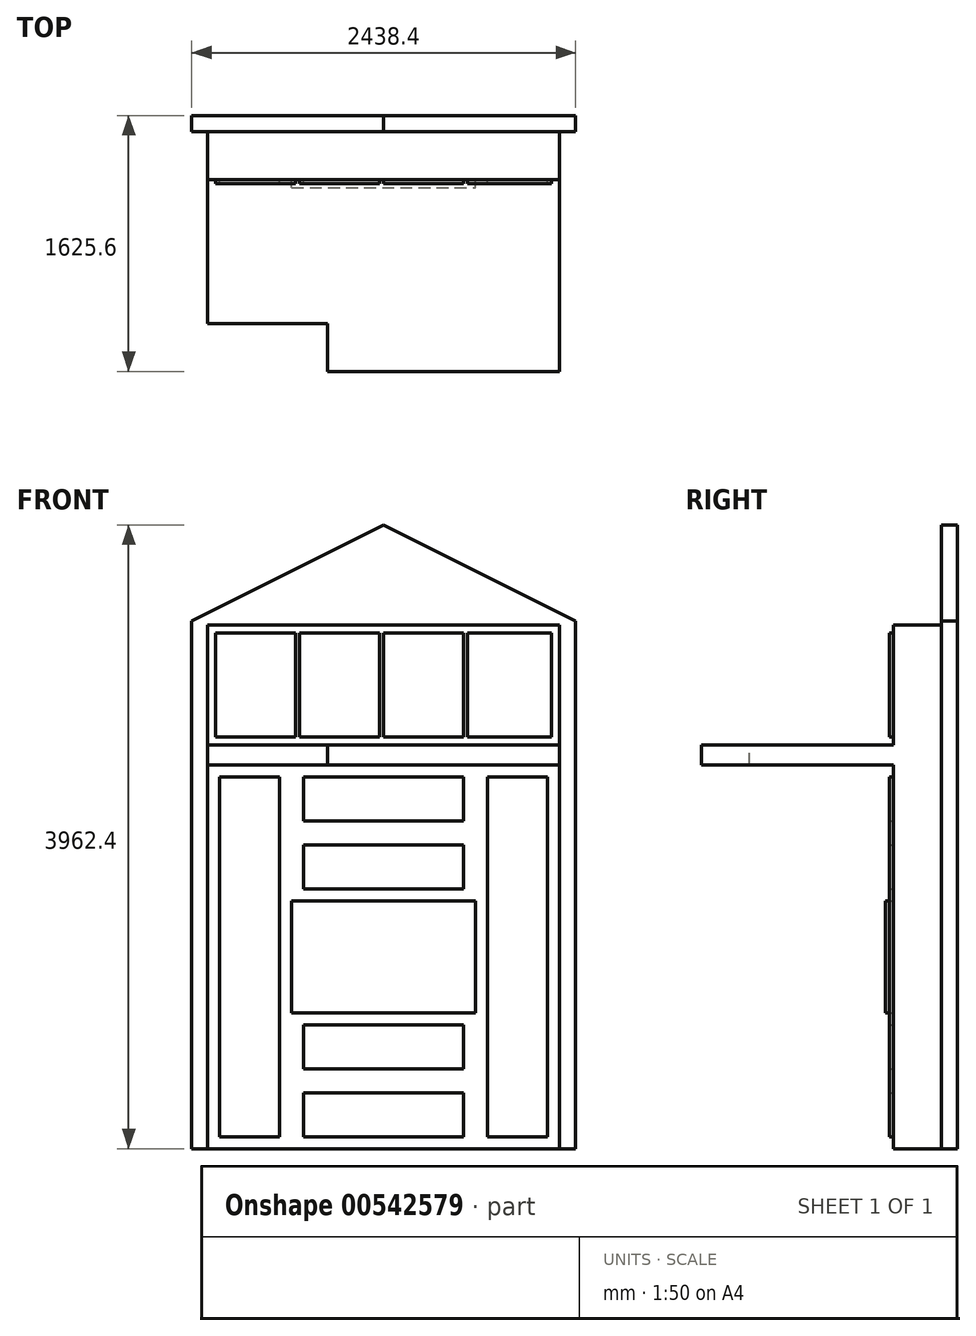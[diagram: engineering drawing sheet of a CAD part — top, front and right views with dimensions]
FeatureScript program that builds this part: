
annotation { "Feature Type Name" : "Feature", "Feature Type Description" : "" }
export const myFeature = defineFeature(function(context is Context, id is Id, definition is map)
    precondition{}
    {
        {
            var Q0;
            Q0=qCreatedBy(makeId("Front.planeOp"),FACE);
            var sketch = newSketch(context, id + "F0", { "sketchPlane" : qUnion([Q0])});
            skLineSegment(sketch, "E0.bottom", {"start": v(0, 0) * mm, "end": v(-2438.4, 0) * mm});
            skLineSegment(sketch, "E0.top", {"start": v(0, 3352.8) * mm, "end": v(-2438.4, 3352.8) * mm});
            skLineSegment(sketch, "E0.left", {"start": v(0, 0) * mm, "end": v(0, 3352.8) * mm});
            skLineSegment(sketch, "E0.right", {"start": v(-2438.4, 0) * mm, "end": v(-2438.4, 3352.8) * mm});
            skPoint(sketch, "E1", {"position": v(-2438.4, 2438.4) * mm});
            skLineSegment(sketch, "E2.bottom", {"start": v(-2438.4, 3352.8) * mm, "end": v(0, 3352.8) * mm, "construction": true});
            skLineSegment(sketch, "E2.top", {"start": v(-2438.4, 3962.4) * mm, "end": v(0, 3962.4) * mm, "construction": true});
            skLineSegment(sketch, "E2.left", {"start": v(-2438.4, 3352.8) * mm, "end": v(-2438.4, 3962.4) * mm, "construction": true});
            skLineSegment(sketch, "E2.right", {"start": v(0, 3352.8) * mm, "end": v(0, 3962.4) * mm, "construction": true});
            skPoint(sketch, "E3", {"position": v(-1219.2, 3962.4) * mm});
            skLineSegment(sketch, "E4", {"start": v(-2438.4, 3352.8) * mm, "end": v(-1219.2, 3962.4) * mm});
            skLineSegment(sketch, "E5", {"start": v(0, 3352.8) * mm, "end": v(-1219.2, 3962.4) * mm});
            skSolve(sketch);
        }
        {
            var Q0;
            Q0=makeQuery(id+"F0.imprint","IMPRINT",FACE,{"disambiguationData":[TD([[makeQuery(id+"F0.imprint","IMPRINT",EDGE,{"derivedFrom":sQuery(id+"F0.wireOp",EDGE,"E0.bottom")}),-1.0]])]});
            var Q1;
            Q1=makeQuery(id+"F0.imprint","IMPRINT",FACE,{"disambiguationData":[TD([[makeQuery(id+"F0.imprint","IMPRINT",EDGE,{"derivedFrom":sQuery(id+"F0.wireOp",EDGE,"E0.top")}),-1.0]])]});
            extrude(context, id + "F1", {"entities" : qUnion([Q0, Q1]), "oppositeDirection" : true, "depth" : 101.6 * mm, "offsetDistance" : 30.48 * mm});
        }
        {
            var Q0;
            Q0=makeQuery(id+"F1.opExtrude","CAP_FACE",FACE,{"disambiguationData":[OSD([sQuery(id+"F0.wireOp",EDGE,"E0.bottom"),sQuery(id+"F0.wireOp",EDGE,"E0.left"),sQuery(id+"F0.wireOp",EDGE,"E0.right"),sQuery(id+"F0.wireOp",EDGE,"E4"),sQuery(id+"F0.wireOp",EDGE,"E5")])],"isStart":true});
            var sketch = newSketch(context, id + "F2", { "sketchPlane" : qUnion([Q0])});
            skLineSegment(sketch, "E6.bottom", {"start": v(-2438.4, 0) * mm, "end": v(0, 0) * mm, "construction": true});
            skLineSegment(sketch, "E6.top", {"start": v(-2438.4, 0) * mm, "end": v(0, 0) * mm, "construction": true});
            skLineSegment(sketch, "E6.left", {"start": v(-2438.4, 0) * mm, "end": v(-2438.4, 0) * mm});
            skLineSegment(sketch, "E6.right", {"start": v(0, 0) * mm, "end": v(0, 0) * mm});
            skLineSegment(sketch, "E7", {"start": v(-2438.4, 2438.4) * mm, "end": v(-2336.8, 2438.4) * mm, "construction": true});
            skLineSegment(sketch, "E8", {"start": v(0, 1378.48) * mm, "end": v(-101.6, 1378.48) * mm, "construction": true});
            skLineSegment(sketch, "E9.bottom", {"start": v(-2336.8, 2438.4) * mm, "end": v(-101.6, 2438.4) * mm});
            skLineSegment(sketch, "E9.top", {"start": v(-2336.8, 0) * mm, "end": v(-101.6, 0) * mm});
            skLineSegment(sketch, "E9.left", {"start": v(-2336.8, 2438.4) * mm, "end": v(-2336.8, 0) * mm});
            skLineSegment(sketch, "E9.right", {"start": v(-101.6, 2438.4) * mm, "end": v(-101.6, 0) * mm});
            skSolve(sketch);
        }
        {
            var Q0;
            Q0=makeQuery(id+"F2.imprint","IMPRINT",FACE,{"disambiguationData":[TD([[makeQuery(id+"F2.imprint","IMPRINT",EDGE,{"derivedFrom":sQuery(id+"F2.wireOp",EDGE,"E9.bottom")}),-1.0]])]});
            extrude(context, id + "F3", {"entities" : qUnion([Q0]), "operationType" : NewBodyOperationType.ADD, "depth" : 304.8 * mm, "offsetDistance" : 30.48 * mm});
        }
        {
            var Q0;
            Q0=makeQuery(id+"F3.opExtrude","CAP_FACE",FACE,{"disambiguationData":[OSD([sQuery(id+"F2.wireOp",EDGE,"E9.bottom"),sQuery(id+"F2.wireOp",EDGE,"E9.top"),sQuery(id+"F2.wireOp",EDGE,"E9.left"),sQuery(id+"F2.wireOp",EDGE,"E9.right")])],"isStart":false});
            var sketch = newSketch(context, id + "F4", { "sketchPlane" : qUnion([Q0])});
            skLineSegment(sketch, "E10", {"start": v(-1219.2, 0) * mm, "end": v(-1219.2, 2438.4) * mm, "construction": true});
            skLineSegment(sketch, "E11", {"start": v(-2336.8, 1219.2) * mm, "end": v(-101.6, 1219.2) * mm, "construction": true});
            skLineSegment(sketch, "E12.bottom", {"start": v(-1803.4, 1574.8) * mm, "end": v(-635, 1574.8) * mm});
            skLineSegment(sketch, "E12.top", {"start": v(-1803.4, 863.6) * mm, "end": v(-635, 863.6) * mm});
            skLineSegment(sketch, "E12.left", {"start": v(-1803.4, 1574.8) * mm, "end": v(-1803.4, 863.6) * mm});
            skLineSegment(sketch, "E12.right", {"start": v(-635, 1574.8) * mm, "end": v(-635, 863.6) * mm});
            skPoint(sketch, "E12.middle", {"position": v(-1219.2, 1219.2) * mm});
            skSolve(sketch);
        }
        {
            var Q0;
            Q0=makeQuery(id+"F4.imprint","IMPRINT",FACE,{"disambiguationData":[TD([[makeQuery(id+"F4.imprint","IMPRINT",EDGE,{"derivedFrom":sQuery(id+"F4.wireOp",EDGE,"E12.bottom")}),-1.0]])]});
            extrude(context, id + "F5", {"entities" : qUnion([Q0]), "operationType" : NewBodyOperationType.ADD, "depth" : 50.8 * mm, "offsetDistance" : 30.48 * mm});
        }
        {
            var Q0;
            Q0=makeQuery(id+"F3.opExtrude","CAP_FACE",FACE,{"disambiguationData":[OSD([sQuery(id+"F2.wireOp",EDGE,"E9.bottom"),sQuery(id+"F2.wireOp",EDGE,"E9.top"),sQuery(id+"F2.wireOp",EDGE,"E9.left"),sQuery(id+"F2.wireOp",EDGE,"E9.right")])],"isStart":false});
            var sketch = newSketch(context, id + "F6", { "sketchPlane" : qUnion([Q0])});
            skLineSegment(sketch, "E13.bottom", {"start": v(-2336.8, 2438.4) * mm, "end": v(-101.6, 2438.4) * mm});
            skLineSegment(sketch, "E13.top", {"start": v(-2336.8, 0) * mm, "end": v(-101.6, 0) * mm});
            skLineSegment(sketch, "E13.left", {"start": v(-2336.8, 2438.4) * mm, "end": v(-2336.8, 0) * mm});
            skLineSegment(sketch, "E13.right", {"start": v(-101.6, 2438.4) * mm, "end": v(-101.6, 0) * mm});
            skLineSegment(sketch, "E14.bottom", {"start": v(-2336.8, 2438.4) * mm, "end": v(-1803.4, 2438.4) * mm, "construction": true});
            skLineSegment(sketch, "E14.top", {"start": v(-2336.8, 0) * mm, "end": v(-1803.4, 0) * mm, "construction": true});
            skLineSegment(sketch, "E14.left", {"start": v(-2336.8, 2438.4) * mm, "end": v(-2336.8, 0) * mm, "construction": true});
            skLineSegment(sketch, "E14.right", {"start": v(-1803.4, 2438.4) * mm, "end": v(-1803.4, 0) * mm});
            skLineSegment(sketch, "E15.bottom", {"start": v(-101.6, 0) * mm, "end": v(-635, 0) * mm});
            skLineSegment(sketch, "E15.top", {"start": v(-101.6, 2438.4) * mm, "end": v(-635, 2438.4) * mm});
            skLineSegment(sketch, "E15.left", {"start": v(-101.6, 0) * mm, "end": v(-101.6, 2438.4) * mm});
            skLineSegment(sketch, "E15.right", {"start": v(-635, 0) * mm, "end": v(-635, 2438.4) * mm});
            skLineSegment(sketch, "E16.bottom", {"start": v(-1803.4, 2438.4) * mm, "end": v(-635, 2438.4) * mm});
            skLineSegment(sketch, "E16.top", {"start": v(-1803.4, 2006.6) * mm, "end": v(-635, 2006.6) * mm});
            skLineSegment(sketch, "E16.left", {"start": v(-1803.4, 2438.4) * mm, "end": v(-1803.4, 2006.6) * mm});
            skLineSegment(sketch, "E16.right", {"start": v(-635, 2438.4) * mm, "end": v(-635, 2006.6) * mm, "construction": true});
            skLineSegment(sketch, "E17.bottom", {"start": v(-1803.4, 863.6) * mm, "end": v(-635, 863.6) * mm, "construction": true});
            skLineSegment(sketch, "E17.top", {"start": v(-1803.4, 431.8) * mm, "end": v(-635, 431.8) * mm});
            skLineSegment(sketch, "E17.left", {"start": v(-1803.4, 863.6) * mm, "end": v(-1803.4, 431.8) * mm});
            skLineSegment(sketch, "E17.right", {"start": v(-635, 863.6) * mm, "end": v(-635, 431.8) * mm});
            skLineSegment(sketch, "E18.0", {"start": v(-1879.6, 2362.2) * mm, "end": v(-1879.6, 76.2) * mm});
            skLineSegment(sketch, "E18.1", {"start": v(-2260.6, 2362.2) * mm, "end": v(-1879.6, 2362.2) * mm});
            skLineSegment(sketch, "E18.2", {"start": v(-2260.6, 2362.2) * mm, "end": v(-2260.6, 76.2) * mm});
            skLineSegment(sketch, "E18.3", {"start": v(-2260.6, 76.2) * mm, "end": v(-1879.6, 76.2) * mm});
            skPoint(sketch, "E19", {"position": v(-635, 431.8) * mm});
            skPoint(sketch, "E20", {"position": v(-635, 863.6) * mm});
            skPoint(sketch, "E21", {"position": v(-635, 2006.6) * mm});
            skPoint(sketch, "E22", {"position": v(-635, 1574.8) * mm});
            skLineSegment(sketch, "E23.bottom", {"start": v(-1727.2, 2362.2) * mm, "end": v(-711.2, 2362.2) * mm});
            skLineSegment(sketch, "E23.top", {"start": v(-1727.2, 2082.8) * mm, "end": v(-711.2, 2082.8) * mm});
            skLineSegment(sketch, "E23.left", {"start": v(-1727.2, 2362.2) * mm, "end": v(-1727.2, 2082.8) * mm});
            skLineSegment(sketch, "E23.right", {"start": v(-711.2, 2362.2) * mm, "end": v(-711.2, 2082.8) * mm});
            skLineSegment(sketch, "E24.bottom", {"start": v(-1727.2, 1930.4) * mm, "end": v(-711.2, 1930.4) * mm});
            skLineSegment(sketch, "E24.top", {"start": v(-1727.2, 1651) * mm, "end": v(-711.2, 1651) * mm});
            skLineSegment(sketch, "E24.left", {"start": v(-1727.2, 1930.4) * mm, "end": v(-1727.2, 1651) * mm});
            skLineSegment(sketch, "E24.right", {"start": v(-711.2, 1930.4) * mm, "end": v(-711.2, 1651) * mm});
            skLineSegment(sketch, "E25.bottom", {"start": v(-177.8, 2362.2) * mm, "end": v(-558.8, 2362.2) * mm});
            skLineSegment(sketch, "E25.top", {"start": v(-177.8, 76.2) * mm, "end": v(-558.8, 76.2) * mm});
            skLineSegment(sketch, "E25.left", {"start": v(-177.8, 2362.2) * mm, "end": v(-177.8, 76.2) * mm});
            skLineSegment(sketch, "E25.right", {"start": v(-558.8, 2362.2) * mm, "end": v(-558.8, 76.2) * mm});
            skLineSegment(sketch, "E26.bottom", {"start": v(-711.2, 76.2) * mm, "end": v(-1727.2, 76.2) * mm});
            skLineSegment(sketch, "E26.top", {"start": v(-711.2, 355.6) * mm, "end": v(-1727.2, 355.6) * mm});
            skLineSegment(sketch, "E26.left", {"start": v(-711.2, 76.2) * mm, "end": v(-711.2, 355.6) * mm});
            skLineSegment(sketch, "E26.right", {"start": v(-1727.2, 76.2) * mm, "end": v(-1727.2, 355.6) * mm});
            skLineSegment(sketch, "E27.bottom", {"start": v(-1727.2, 787.4) * mm, "end": v(-711.2, 787.4) * mm});
            skLineSegment(sketch, "E27.top", {"start": v(-1727.2, 508) * mm, "end": v(-711.2, 508) * mm});
            skLineSegment(sketch, "E27.left", {"start": v(-1727.2, 787.4) * mm, "end": v(-1727.2, 508) * mm});
            skLineSegment(sketch, "E27.right", {"start": v(-711.2, 787.4) * mm, "end": v(-711.2, 508) * mm});
            skSolve(sketch);
        }
        {
            var Q0;
            Q0=makeQuery(id+"F6.imprint","IMPRINT",FACE,{"disambiguationData":[TD([[makeQuery(id+"F6.imprint","IMPRINT",EDGE,{"derivedFrom":sQuery(id+"F6.wireOp",EDGE,"E25.bottom")}),1.0]])]});
            var Q1;
            Q1=makeQuery(id+"F6.imprint","IMPRINT",FACE,{"disambiguationData":[TD([[makeQuery(id+"F6.imprint","IMPRINT",EDGE,{"derivedFrom":sQuery(id+"F6.wireOp",EDGE,"E23.bottom")}),-1.0]])]});
            var Q2;
            Q2=makeQuery(id+"F6.imprint","IMPRINT",FACE,{"disambiguationData":[TD([[makeQuery(id+"F6.imprint","IMPRINT",EDGE,{"derivedFrom":sQuery(id+"F6.wireOp",EDGE,"E24.bottom")}),-1.0]])]});
            var Q3;
            Q3=makeQuery(id+"F6.imprint","IMPRINT",FACE,{"disambiguationData":[TD([[makeQuery(id+"F6.imprint","IMPRINT",EDGE,{"derivedFrom":sQuery(id+"F6.wireOp",EDGE,"E18.0")}),-1.0]])]});
            var Q4;
            Q4=makeQuery(id+"F6.imprint","IMPRINT",FACE,{"disambiguationData":[TD([[makeQuery(id+"F6.imprint","IMPRINT",EDGE,{"derivedFrom":sQuery(id+"F6.wireOp",EDGE,"E27.bottom")}),-1.0]])]});
            var Q5;
            Q5=makeQuery(id+"F6.imprint","IMPRINT",FACE,{"disambiguationData":[TD([[makeQuery(id+"F6.imprint","IMPRINT",EDGE,{"derivedFrom":sQuery(id+"F6.wireOp",EDGE,"E26.bottom")}),-1.0]])]});
            extrude(context, id + "F7", {"entities" : qUnion([Q0, Q1, Q2, Q3, Q4, Q5]), "operationType" : NewBodyOperationType.ADD, "depth" : 25.4 * mm, "offsetDistance" : 30.48 * mm});
        }
        {
            var Q0;
            Q0=makeQuery(id+"F1.opExtrude","CAP_FACE",FACE,{"disambiguationData":[OSD([sQuery(id+"F0.wireOp",EDGE,"E0.bottom"),sQuery(id+"F0.wireOp",EDGE,"E0.left"),sQuery(id+"F0.wireOp",EDGE,"E0.right"),sQuery(id+"F0.wireOp",EDGE,"E4"),sQuery(id+"F0.wireOp",EDGE,"E5")])],"isStart":true});
            var sketch = newSketch(context, id + "F8", { "sketchPlane" : qUnion([Q0])});
            skLineSegment(sketch, "E28.bottom", {"start": v(-2336.8, 2438.4) * mm, "end": v(-101.6, 2438.4) * mm});
            skLineSegment(sketch, "E28.top", {"start": v(-2336.8, 2565.4) * mm, "end": v(-101.6, 2565.4) * mm});
            skLineSegment(sketch, "E28.left", {"start": v(-2336.8, 2438.4) * mm, "end": v(-2336.8, 2565.4) * mm});
            skLineSegment(sketch, "E28.right", {"start": v(-101.6, 2438.4) * mm, "end": v(-101.6, 2565.4) * mm});
            skLineSegment(sketch, "E29.top", {"start": v(-2336.8, 3327.4) * mm, "end": v(-101.6, 3327.4) * mm});
            skLineSegment(sketch, "E29.left", {"start": v(-2336.8, 2565.4) * mm, "end": v(-2336.8, 3327.4) * mm});
            skLineSegment(sketch, "E29.right", {"start": v(-101.6, 2565.4) * mm, "end": v(-101.6, 3327.4) * mm});
            skSolve(sketch);
        }
        {
            var Q0;
            Q0=makeQuery(id+"F8.imprint","IMPRINT",FACE,{"disambiguationData":[TD([[makeQuery(id+"F8.imprint","IMPRINT",EDGE,{"derivedFrom":sQuery(id+"F8.wireOp",EDGE,"E28.bottom")}),1.0]])]});
            extrude(context, id + "F9", {"entities" : qUnion([Q0]), "operationType" : NewBodyOperationType.ADD, "depth" : 1219.2 * mm, "offsetDistance" : 25.4 * mm});
        }
        {
            var Q0;
            Q0=makeQuery(id+"F8.imprint","IMPRINT",FACE,{"disambiguationData":[TD([[makeQuery(id+"F8.imprint","IMPRINT",EDGE,{"derivedFrom":sQuery(id+"F8.wireOp",EDGE,"E28.top")}),1.0]])]});
            extrude(context, id + "F10", {"entities" : qUnion([Q0]), "operationType" : NewBodyOperationType.ADD, "depth" : 304.8 * mm, "offsetDistance" : 25.4 * mm});
        }
        {
            var Q0;
            Q0=makeQuery(id+"F10.opExtrude","CAP_FACE",FACE,{"disambiguationData":[OSD([sQuery(id+"F8.wireOp",EDGE,"E28.top"),sQuery(id+"F8.wireOp",EDGE,"E29.top"),sQuery(id+"F8.wireOp",EDGE,"E29.left"),sQuery(id+"F8.wireOp",EDGE,"E29.right")])],"isStart":false});
            var sketch = newSketch(context, id + "F11", { "sketchPlane" : qUnion([Q0])});
            skLineSegment(sketch, "E30.0", {"start": v(-2286, 3276.6) * mm, "end": v(-2286, 2616.2) * mm});
            skLineSegment(sketch, "E30.1", {"start": v(-152.4, 3276.6) * mm, "end": v(-2286, 3276.6) * mm});
            skLineSegment(sketch, "E30.2", {"start": v(-152.4, 2616.2) * mm, "end": v(-152.4, 3276.6) * mm});
            skLineSegment(sketch, "E30.3", {"start": v(-2286, 2616.2) * mm, "end": v(-152.4, 2616.2) * mm});
            skLineSegment(sketch, "E31", {"start": v(-1219.2, 3276.6) * mm, "end": v(-1219.2, 2616.2) * mm});
            skLineSegment(sketch, "E32", {"start": v(-1752.6, 3276.6) * mm, "end": v(-1752.6, 2616.2) * mm});
            skLineSegment(sketch, "E33", {"start": v(-685.8, 2616.2) * mm, "end": v(-685.8, 3276.6) * mm});
            skLineSegment(sketch, "E34.0", {"start": v(-1778, 3276.6) * mm, "end": v(-1778, 2616.2) * mm});
            skLineSegment(sketch, "E35.0", {"start": v(-1244.6, 3276.6) * mm, "end": v(-1244.6, 2616.2) * mm});
            skLineSegment(sketch, "E36.0", {"start": v(-711.2, 2616.2) * mm, "end": v(-711.2, 3276.6) * mm});
            skSolve(sketch);
        }
        {
            var Q0;
            {var subQ0=sQuery(id+"F11.wireOp",EDGE,"E30.0");Q0=makeQuery(id+"F11.imprint","IMPRINT",FACE,{"disambiguationData":[TD([[makeQuery(id+"F11.imprint","IMPRINT",EDGE,{"derivedFrom":subQ0}),1.0]])]});}
            var Q1;
            {var subQ0=sQuery(id+"F11.wireOp",EDGE,"E32");Q1=makeQuery(id+"F11.imprint","IMPRINT",FACE,{"disambiguationData":[TD([[makeQuery(id+"F11.imprint","IMPRINT",EDGE,{"derivedFrom":subQ0}),1.0]])]});}
            var Q2;
            {var subQ0=sQuery(id+"F11.wireOp",EDGE,"E31");Q2=makeQuery(id+"F11.imprint","IMPRINT",FACE,{"disambiguationData":[TD([[makeQuery(id+"F11.imprint","IMPRINT",EDGE,{"derivedFrom":subQ0}),1.0]])]});}
            var Q3;
            {var subQ0=sQuery(id+"F11.wireOp",EDGE,"E30.2");Q3=makeQuery(id+"F11.imprint","IMPRINT",FACE,{"disambiguationData":[TD([[makeQuery(id+"F11.imprint","IMPRINT",EDGE,{"derivedFrom":subQ0}),1.0]])]});}
            extrude(context, id + "F12", {"entities" : qUnion([Q0, Q1, Q2, Q3]), "operationType" : NewBodyOperationType.ADD, "depth" : 25.4 * mm, "offsetDistance" : 25.4 * mm});
        }
        {
            var Q0;
            Q0=makeQuery(id+"F9.opExtrude","CAP_FACE",FACE,{"disambiguationData":[OSD([sQuery(id+"F8.wireOp",EDGE,"E28.bottom"),sQuery(id+"F8.wireOp",EDGE,"E28.left"),sQuery(id+"F8.wireOp",EDGE,"E28.right"),sQuery(id+"F8.wireOp",EDGE,"E28.top")])],"isStart":false});
            var sketch = newSketch(context, id + "F13", { "sketchPlane" : qUnion([Q0])});
            skLineSegment(sketch, "E37", {"start": v(-1574.8, 2438.4) * mm, "end": v(-1574.8, 2565.4) * mm});
            skSolve(sketch);
        }
        {
            var Q0;
            {var subQ0=sQuery(id+"F13.wireOp",EDGE,"E37");Q0=makeQuery(id+"F13.imprint","IMPRINT",FACE,{"disambiguationData":[TD([[makeQuery(id+"F13.imprint","IMPRINT",EDGE,{"derivedFrom":subQ0}),-1.0]])]});}
            extrude(context, id + "F14", {"entities" : qUnion([Q0]), "operationType" : NewBodyOperationType.ADD, "depth" : 304.8 * mm, "offsetDistance" : 25.4 * mm});
        }
    });
